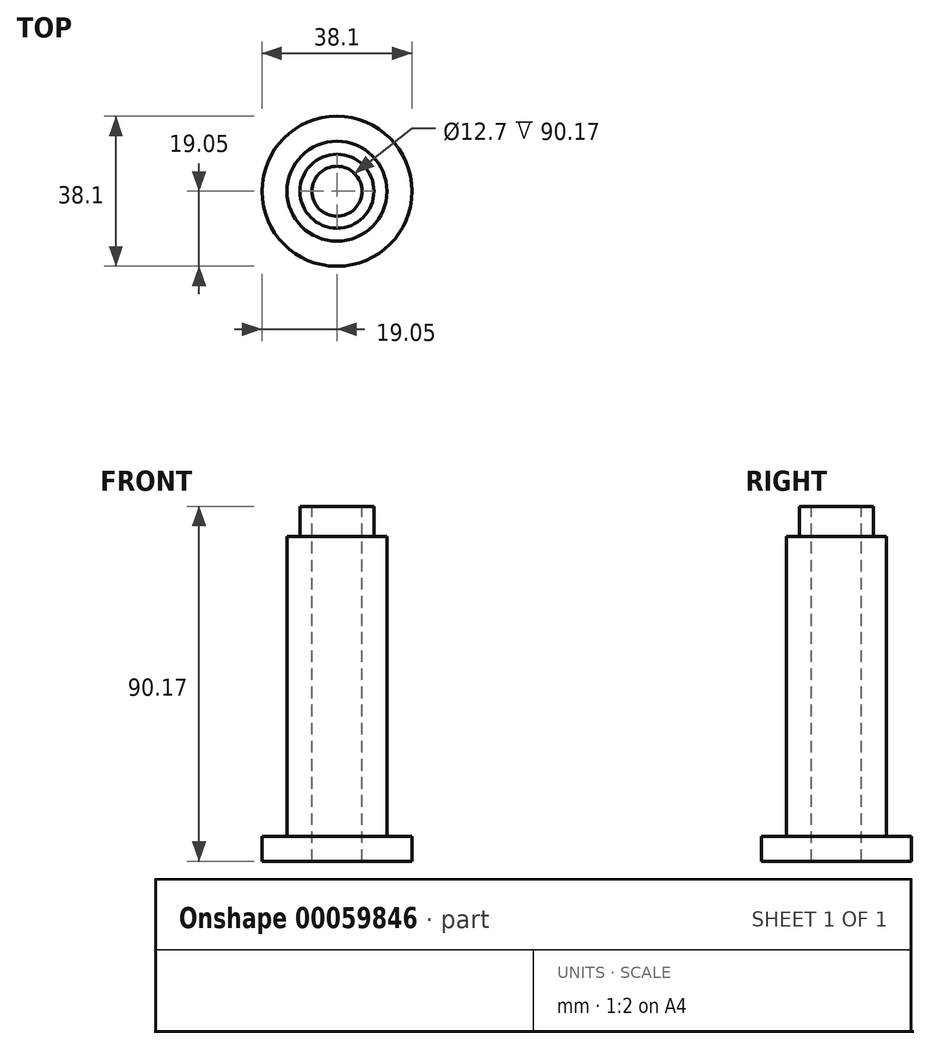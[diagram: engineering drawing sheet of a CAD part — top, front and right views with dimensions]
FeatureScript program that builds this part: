
annotation { "Feature Type Name" : "Feature", "Feature Type Description" : "" }
export const myFeature = defineFeature(function(context is Context, id is Id, definition is map)
    precondition{}
    {
        {
            var Q0;
            Q0=qCreatedBy(makeId("Top.planeOp"),FACE);
            var sketch = newSketch(context, id + "F0", { "sketchPlane" : qUnion([Q0])});
            skCircle(sketch, "E0", {"center": v(0, 0) * mm, "radius": 19.05 * mm});
            skSolve(sketch);
        }
        {
            var Q0;
            Q0=makeQuery(id+"F0.imprint","IMPRINT",FACE,{"disambiguationData":[TD([[makeQuery(id+"F0.imprint","IMPRINT",EDGE,{"derivedFrom":sQuery(id+"F0.wireOp",EDGE,"E0")}),1.0]])]});
            extrude(context, id + "F1", {"entities" : qUnion([Q0]), "depth" : 6.35 * mm});
        }
        {
            var Q0;
            Q0=makeQuery(id+"F1.opExtrude","CAP_FACE",FACE,{"disambiguationData":[OSD([sQuery(id+"F0.wireOp",EDGE,"E0")])],"isStart":false});
            var sketch = newSketch(context, id + "F2", { "sketchPlane" : qUnion([Q0])});
            skCircle(sketch, "E1", {"center": v(0, 0) * mm, "radius": 12.7 * mm});
            skSolve(sketch);
        }
        {
            var Q0;
            Q0=makeQuery(id+"F2.imprint","IMPRINT",FACE,{"disambiguationData":[TD([[makeQuery(id+"F2.imprint","IMPRINT",EDGE,{"derivedFrom":sQuery(id+"F2.wireOp",EDGE,"E1")}),1.0]])]});
            extrude(context, id + "F3", {"entities" : qUnion([Q0]), "operationType" : NewBodyOperationType.ADD, "depth" : 76.2 * mm});
        }
        {
            var Q0;
            Q0=makeQuery(id+"F3.opExtrude","CAP_FACE",FACE,{"disambiguationData":[OSD([sQuery(id+"F2.wireOp",EDGE,"E1")])],"isStart":false});
            var sketch = newSketch(context, id + "F4", { "sketchPlane" : qUnion([Q0])});
            skCircle(sketch, "E2", {"center": v(0, 0) * mm, "radius": 9.4 * mm});
            skSolve(sketch);
        }
        {
            var Q0;
            Q0=makeQuery(id+"F4.imprint","IMPRINT",FACE,{"disambiguationData":[TD([[makeQuery(id+"F4.imprint","IMPRINT",EDGE,{"derivedFrom":sQuery(id+"F4.wireOp",EDGE,"E2")}),1.0]])]});
            extrude(context, id + "F5", {"entities" : qUnion([Q0]), "operationType" : NewBodyOperationType.ADD, "depth" : 7.62 * mm});
        }
        {
            var Q0;
            Q0=makeQuery(id+"F5.opExtrude","CAP_FACE",FACE,{"disambiguationData":[OSD([sQuery(id+"F4.wireOp",EDGE,"E2")])],"isStart":false});
            var sketch = newSketch(context, id + "F6", { "sketchPlane" : qUnion([Q0])});
            skPoint(sketch, "E3", {"position": v(0, 0) * mm});
            skSolve(sketch);
        }
        {
            var Q0;
            Q0=sQuery(id+"F6.wireOp",VERTEX,"E3");
            var Q1;
            Q1=makeQuery(id+"F1.opExtrude","SWEPT_BODY",BODY,{"disambiguationData":[OSD([sQuery(id+"F0.wireOp",EDGE,"E0")])]});
            hole(context, id + "F7", {"style" : HoleStyle.SIMPLE, "holeDiameter" : 12.7 * mm, "endStyle" : HoleEndStyle.THROUGH, "locations" : qUnion([Q0]), "scope" : qUnion([Q1])});
        }
    });
